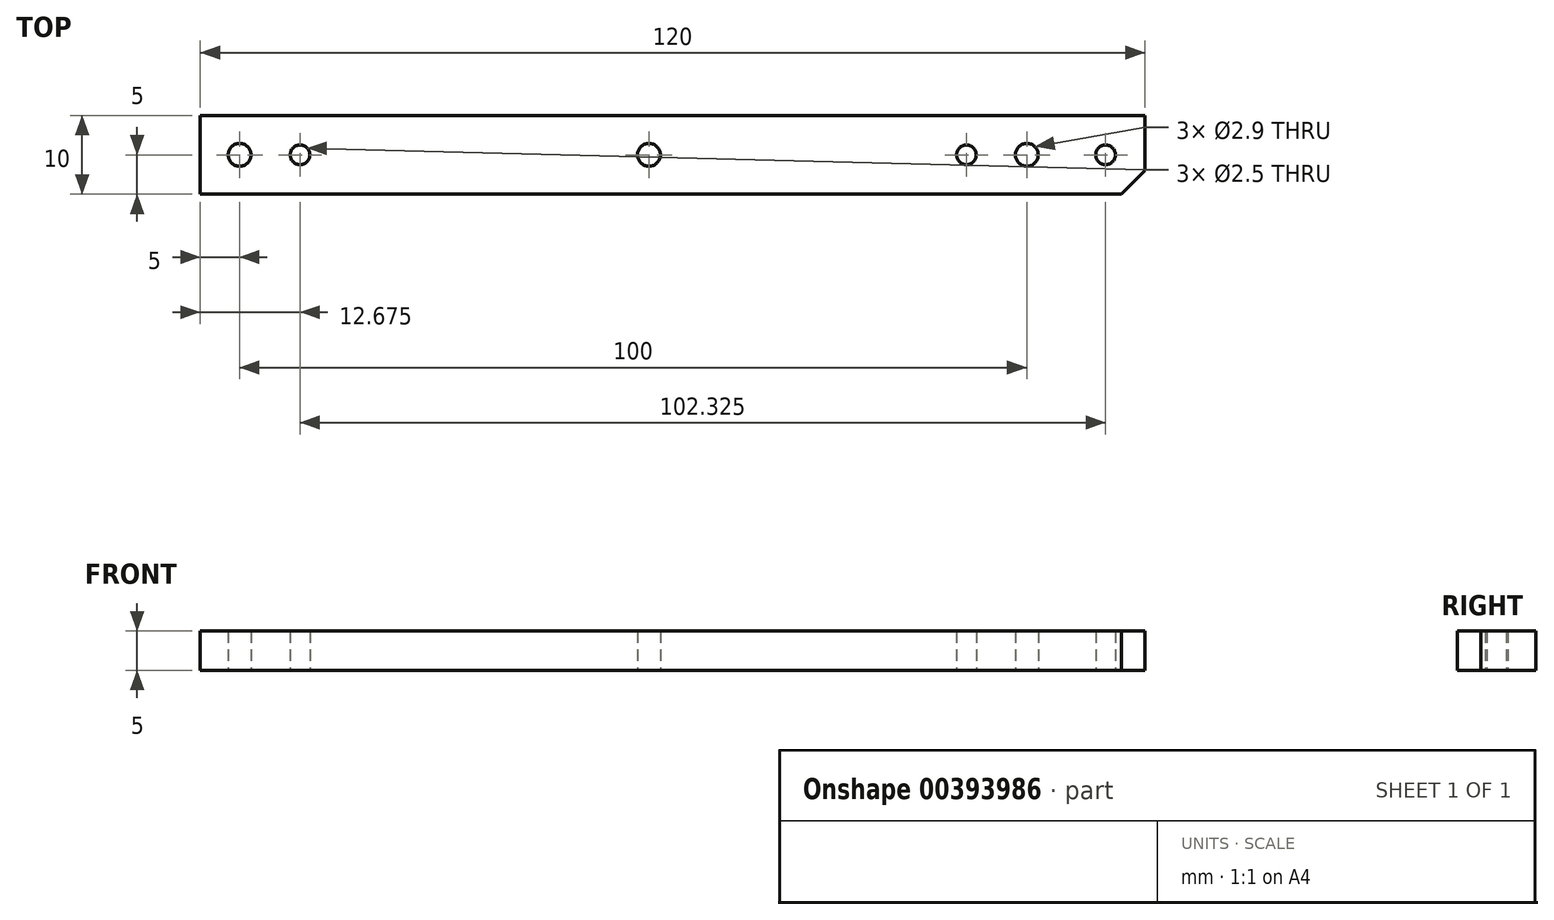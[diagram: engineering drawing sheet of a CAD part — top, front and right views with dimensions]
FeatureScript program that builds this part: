
annotation { "Feature Type Name" : "Feature", "Feature Type Description" : "" }
export const myFeature = defineFeature(function(context is Context, id is Id, definition is map)
    precondition{}
    {
        {
            var Q0;
            Q0=qCreatedBy(makeId("Top.planeOp"),FACE);
            var sketch = newSketch(context, id + "F0", { "sketchPlane" : qUnion([Q0])});
            skLineSegment(sketch, "E0.bottom", {"start": v(65, 5) * mm, "end": v(-55, 5) * mm});
            skLineSegment(sketch, "E0.top", {"start": v(65, -5) * mm, "end": v(-55, -5) * mm});
            skLineSegment(sketch, "E0.right", {"start": v(-55, 5) * mm, "end": v(-55, -5) * mm});
            skPoint(sketch, "E0.middle", {"position": v(0, 0) * mm});
            skCircle(sketch, "E1", {"center": v(-50, 0) * mm, "radius": 1.45 * mm});
            skCircle(sketch, "E2", {"center": v(2, 0) * mm, "radius": 1.45 * mm});
            skLineSegment(sketch, "E3.right", {"start": v(65, 5) * mm, "end": v(65, -5) * mm});
            skCircle(sketch, "E4.MirrorC", {"center": v(50, 0) * mm, "radius": 1.45 * mm});
            skCircle(sketch, "E5", {"center": v(60, 0) * mm, "radius": 1.25 * mm});
            skCircle(sketch, "E6", {"center": v(-42.33, 0) * mm, "radius": 1.25 * mm});
            skCircle(sketch, "E7.MirrorC", {"center": v(42.33, 0) * mm, "radius": 1.25 * mm});
            skSolve(sketch);
        }
        {
            var Q0;
            Q0=qSketchRegion(id+"F0",true);
            extrude(context, id + "F1", {"entities" : qUnion([Q0]), "depth" : 5 * mm});
        }
        {
            var Q0;
            Q0=makeQuery(id+"F1.opExtrude","SWEPT_EDGE",EDGE,{"disambiguationData":[OSD([sQuery(id+"F0.wireOp",EDGE,"E0.top"),sQuery(id+"F0.wireOp",EDGE,"E3.right")])]});
            chamfer(context, id + "F2", {"entities" : qUnion([Q0]), "width" : 3 * mm, "tangentPropagation" : true});
        }
    });
